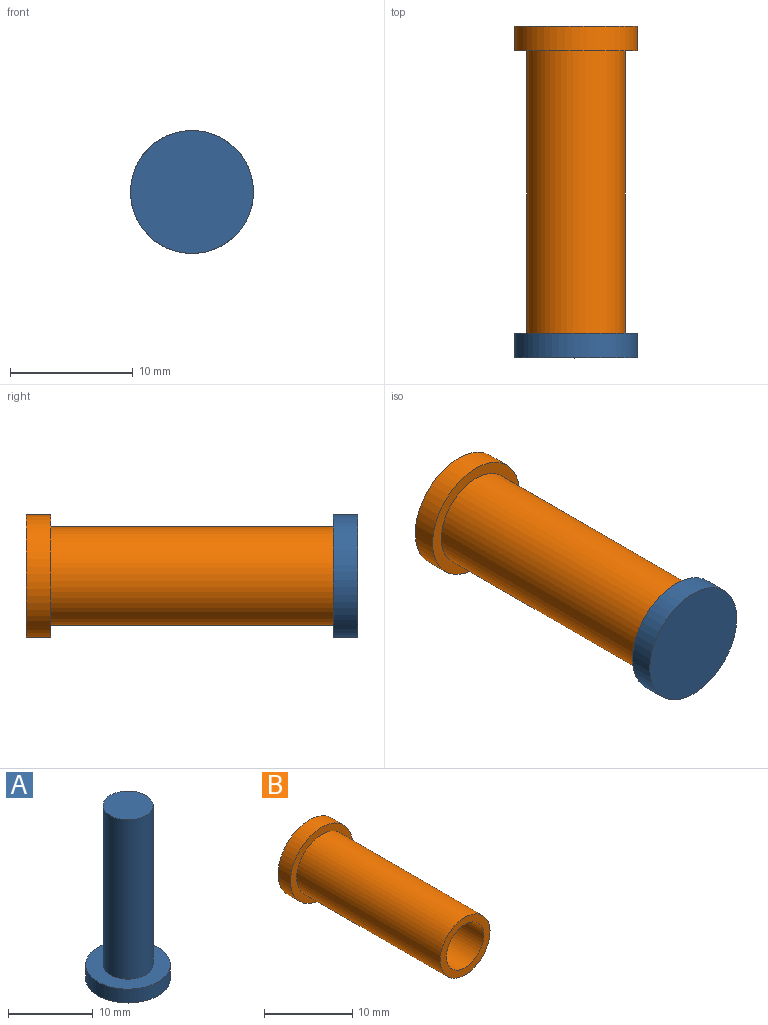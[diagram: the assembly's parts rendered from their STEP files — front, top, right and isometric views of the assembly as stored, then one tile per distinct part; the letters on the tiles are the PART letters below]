
ASSEMBLY  parts=2 mates=1
PART A: 5 faces, bbox 10x10x25 mm
  f0: cylinder r=5mm len=10mm, axis (0,0,-1), area 62.8mm2, adj f1,f2
  f1: plane 10x10mm, normal (0,0,1), area 51.2mm2, adj f0,f3
  f2: plane 10x10mm, normal (0,0,-1), area 78.5mm2, adj f0
  f3: cylinder r=2.95mm len=23mm, axis (0,0,-1), area 426.3mm2, adj f1,f4
  f4: plane 5.9x5.9mm, normal (0,0,1), area 27.3mm2, adj f3
PART B: 7 faces, bbox 10x25x10 mm
  f0: cylinder r=5mm len=10mm, axis (0,1,0), area 62.8mm2, adj f1,f2
  f1: plane 10x10mm, normal (0,-1,0), area 28.3mm2, adj f0,f3
  f2: plane 10x10mm, normal (0,1,0), area 78.5mm2, adj f0
  f3: cylinder r=4mm len=23mm, axis (0,1,0), area 578.1mm2, adj f1,f4
  f4: plane 8x8mm, normal (0,-1,0), area 22mm2, adj f3,f5
  f5: cylinder r=3mm len=23mm, axis (0,-1,0), area 433.5mm2, adj f4,f6
  f6: plane 6x6mm, normal (0,-1,0), area 28.3mm2, adj f5
PLACE A rot(axis=(-1,0,0),90deg) t=(6.2,-26.21,3.69)mm
PLACE B rot(axis=(0,-1,0),0deg) t=(6.2,0.79,3.69)mm fixed
MATE slider A.f3 <-> B.f5  axis (0,1,0) through (6.2,-1.21,3.69)mm
